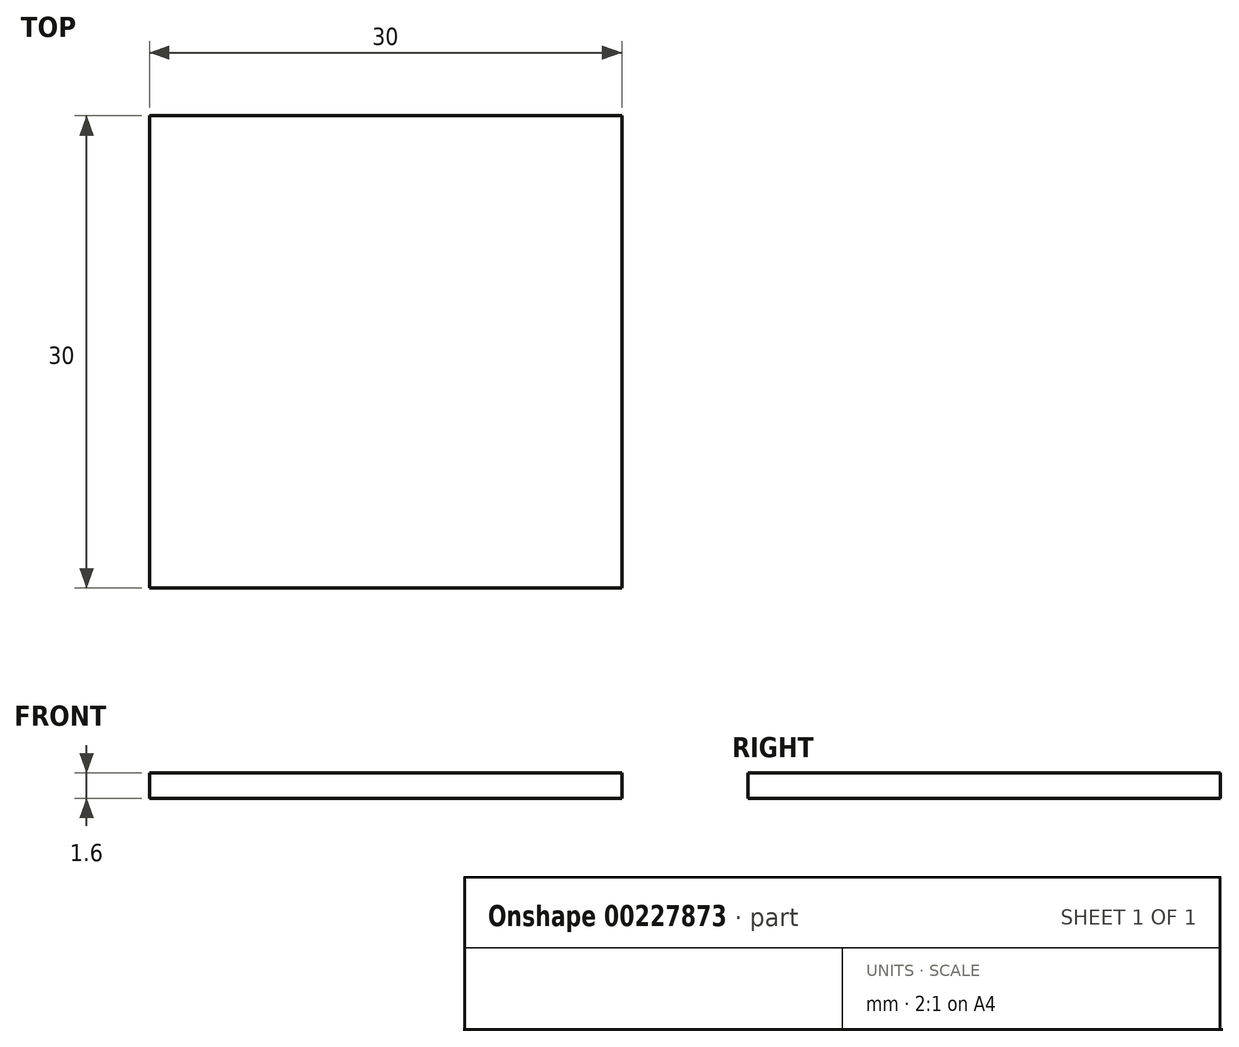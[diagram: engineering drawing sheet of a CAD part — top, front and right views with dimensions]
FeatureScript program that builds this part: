
annotation { "Feature Type Name" : "Feature", "Feature Type Description" : "" }
export const myFeature = defineFeature(function(context is Context, id is Id, definition is map)
    precondition{}
    {
        {
            var Q0;
            Q0=qCreatedBy(makeId("Top.planeOp"),FACE);
            var sketch = newSketch(context, id + "F0", { "sketchPlane" : qUnion([Q0])});
            skPoint(sketch, "E0.middle", {"position": v(0, 0) * mm});
            skLineSegment(sketch, "E1.bottom", {"start": v(-15, 15) * mm, "end": v(15, 15) * mm});
            skLineSegment(sketch, "E1.top", {"start": v(-15, -15) * mm, "end": v(15, -15) * mm});
            skLineSegment(sketch, "E1.left", {"start": v(-15, 15) * mm, "end": v(-15, -15) * mm});
            skLineSegment(sketch, "E1.right", {"start": v(15, 15) * mm, "end": v(15, -15) * mm});
            skPoint(sketch, "E2.visualSharp", {"position": v(-15, 15) * mm});
            skLineSegment(sketch, "E2.filletArc", {"start": v(-15, 15) * mm, "end": v(-15, 15) * mm});
            skPoint(sketch, "E3.visualSharp", {"position": v(15, 15) * mm});
            skLineSegment(sketch, "E3.filletArc", {"start": v(15, 15) * mm, "end": v(15, 15) * mm});
            skPoint(sketch, "E4.visualSharp", {"position": v(15, -15) * mm});
            skLineSegment(sketch, "E4.filletArc", {"start": v(15, -15) * mm, "end": v(15, -15) * mm});
            skLineSegment(sketch, "E5.filletArc", {"start": v(-15, -15) * mm, "end": v(-15, -15) * mm});
            skSolve(sketch);
        }
        {
            var Q0;
            Q0=qSketchRegion(id+"F0",true);
            extrude(context, id + "F1", {"entities" : qUnion([Q0]), "depth" : 1.6 * mm});
        }
    });
